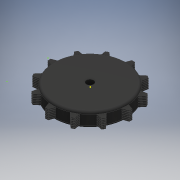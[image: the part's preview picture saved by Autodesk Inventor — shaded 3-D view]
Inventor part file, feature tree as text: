
AUTODESK INVENTOR PART (.ipt)
format: ipt  version: 2018 (Build 220112000, 112)  size: 581,120 bytes
history: native  units: mm
features: sketch x17, extrude x6, fillet x2, pattern_linear x1, pattern_circular x1
ambient origin geometry x8: Origin, YZ Plane, XZ Plane, XY Plane, X Axis, Y Axis, Z Axis, Center Point
bodies: Solid1 (feature_tree)
feature tree (27):
  sketch  "Sketch1"  dims[d0=1000.0mm d1=200.0mm d2=0.0mm]
  sketch  "Sketch2"  dims[d18=10.0mm d19=0.0mm d20=20.0mm d21=0.0mm]
  extrude  "Extrusion1"  Depth=1000.0mm TaperAngle=0.0deg
  extrude  "Extrusion2"  Depth=20.0mm TaperAngle=0.0deg
  sketch  "Sketch4"  dims[d31=200.0mm d32=0.0mm d33=2000.0mm d34=0.0mm]
  sketch  "Sketch5"  dims[d35=30.0mm d36=30.0mm]
  extrude  "Extrusion3"  Depth=120.0mm TaperAngle=360.0deg
  pattern_linear  "Rectangular Pattern1"  Count1=100 Spacing1=0.0mm
  sketch  "Sketch7"
  sketch  "Sketch8"
  sketch  "Sketch9"
  sketch  "Sketch10"
  sketch  "Sketch11"
  pattern_circular  "Circular Pattern1"  Count=10  [1 undecoded]
  extrude  "Extrusion4"  Depth=2000.0mm TaperAngle=0.0deg
  extrude  "Extrusion5"  Depth=30.0mm
  sketch  "Sketch14"
  sketch  "Sketch15"
  extrude  "Extrusion6"  [1 undecoded]
  sketch  "Sketch17"
  fillet  "Fillet1"  [1 undecoded]
  fillet  "Fillet2"  [1 undecoded]
  sketch  "Sketch3"  dims[d22=100.0mm d24=20.0mm d25=120.0mm d26=360.0deg d28=1000.0mm d29=0.0mm d30=100.0mm]
  sketch  "Sketch6"
  sketch  "Sketch12"
  sketch  "Sketch13"
  sketch  "Sketch16"
note: 4 required parameter values undecoded (feature->parameter linkage not recoverable at this tier; creation-order binding heuristic only, values carry confidence <= 0.55)
